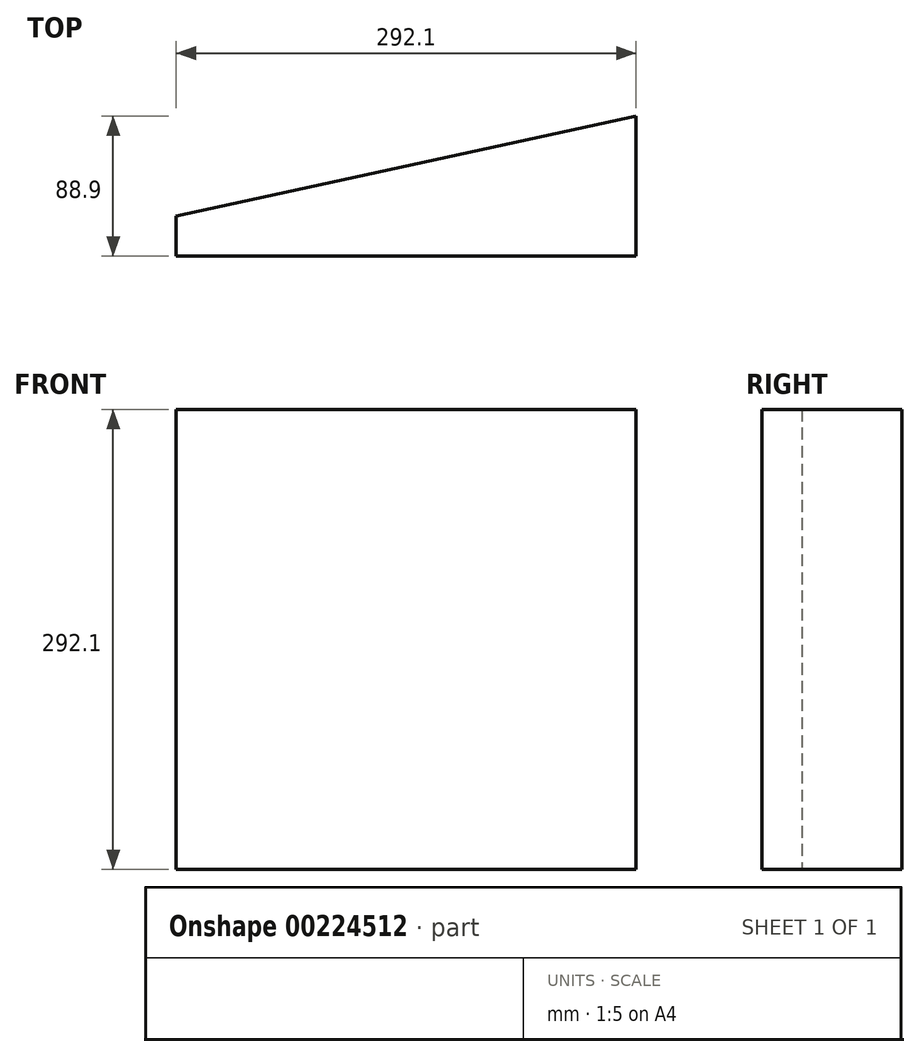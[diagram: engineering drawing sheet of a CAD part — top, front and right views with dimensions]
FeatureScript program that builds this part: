
annotation { "Feature Type Name" : "Feature", "Feature Type Description" : "" }
export const myFeature = defineFeature(function(context is Context, id is Id, definition is map)
    precondition{}
    {
        {
            var Q0;
            Q0=qCreatedBy(makeId("Top.planeOp"),FACE);
            var sketch = newSketch(context, id + "F0", { "sketchPlane" : qUnion([Q0])});
            skLineSegment(sketch, "E0.top", {"start": v(-122.39, -87.2) * mm, "end": v(169.71, -87.2) * mm});
            skLineSegment(sketch, "E0.right", {"start": v(169.71, 1.7) * mm, "end": v(169.71, -87.2) * mm});
            skLineSegment(sketch, "E1", {"start": v(-122.39, -87.2) * mm, "end": v(-122.39, -61.8) * mm});
            skLineSegment(sketch, "E2", {"start": v(-122.39, -61.8) * mm, "end": v(169.71, 1.7) * mm});
            skSolve(sketch);
        }
        {
            var Q0;
            Q0=makeQuery(id+"F0.imprint","IMPRINT",FACE,{"disambiguationData":[TD([[makeQuery(id+"F0.imprint","IMPRINT",EDGE,{"derivedFrom":sQuery(id+"F0.wireOp",EDGE,"E0.top")}),1.0]])]});
            extrude(context, id + "F1", {"entities" : qUnion([Q0]), "depth" : 292.1 * mm});
        }
    });
